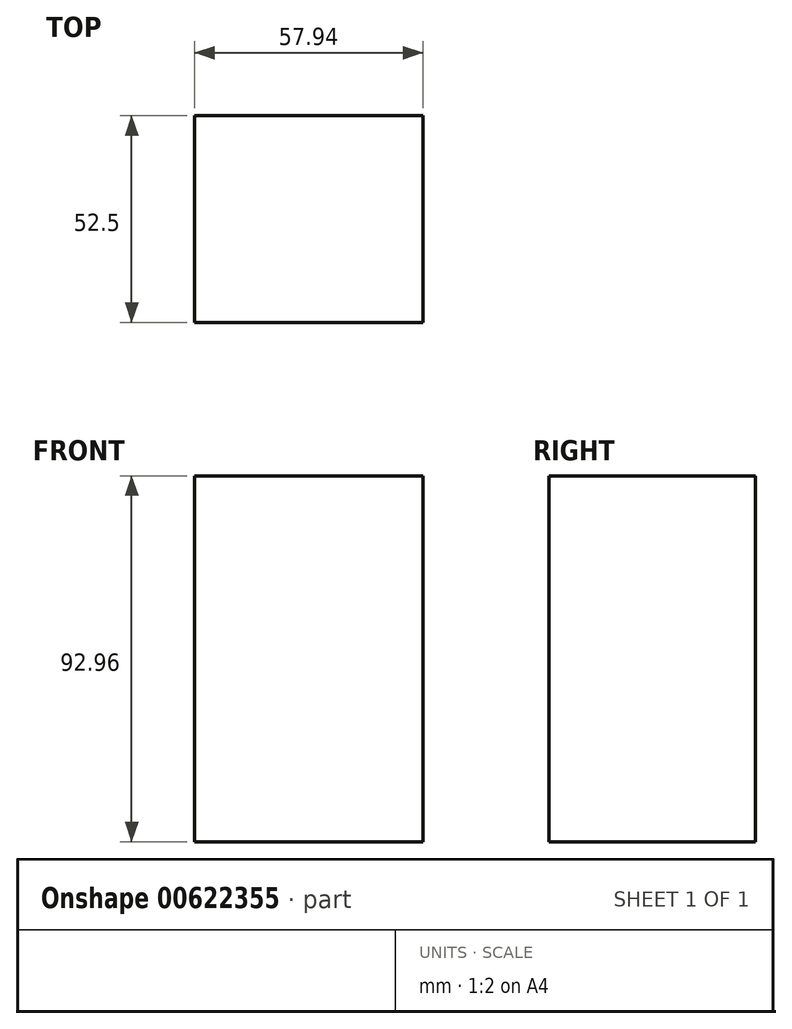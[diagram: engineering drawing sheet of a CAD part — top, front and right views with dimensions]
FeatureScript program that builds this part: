
annotation { "Feature Type Name" : "Feature", "Feature Type Description" : "" }
export const myFeature = defineFeature(function(context is Context, id is Id, definition is map)
    precondition{}
    {
        {
            var Q0;
            Q0=qCreatedBy(makeId("Top.planeOp"),FACE);
            var sketch = newSketch(context, id + "F0", { "sketchPlane" : qUnion([Q0])});
            skLineSegment(sketch, "E0.bottom", {"start": v(0, 0) * mm, "end": v(-57.94, 0) * mm});
            skLineSegment(sketch, "E0.top", {"start": v(0, 52.5) * mm, "end": v(-57.94, 52.5) * mm});
            skLineSegment(sketch, "E0.left", {"start": v(0, 0) * mm, "end": v(0, 52.5) * mm});
            skLineSegment(sketch, "E0.right", {"start": v(-57.94, 0) * mm, "end": v(-57.94, 52.5) * mm});
            skSolve(sketch);
        }
        {
            var Q0;
            Q0=makeQuery(id+"F0.imprint","IMPRINT",FACE,{"disambiguationData":[TD([[makeQuery(id+"F0.imprint","IMPRINT",EDGE,{"derivedFrom":sQuery(id+"F0.wireOp",EDGE,"E0.bottom")}),-1.0]])]});
            extrude(context, id + "F1", {"entities" : qUnion([Q0]), "depth" : 92.96 * mm, "offsetDistance" : 25.4 * mm});
        }
    });
